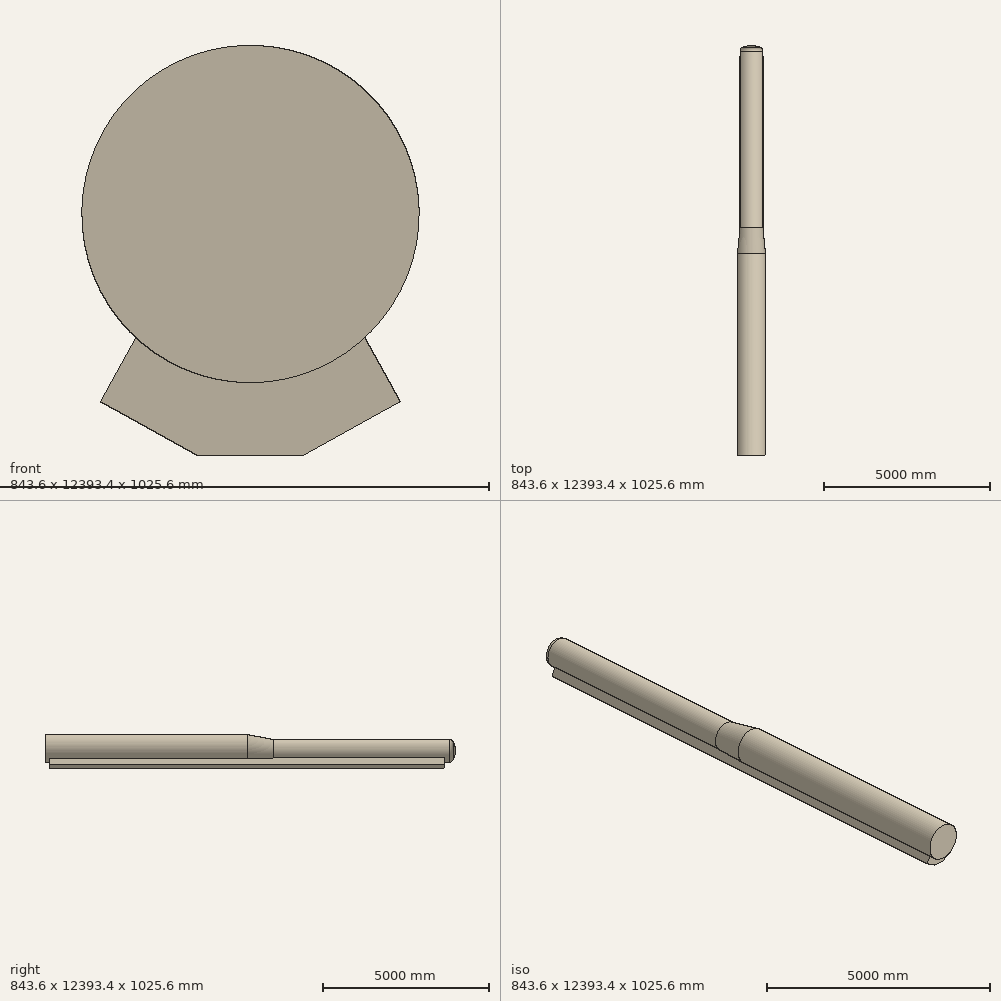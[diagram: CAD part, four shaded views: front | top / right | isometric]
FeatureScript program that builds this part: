
annotation { "Feature Type Name" : "Feature", "Feature Type Description" : "" }
export const myFeature = defineFeature(function(context is Context, id is Id, definition is map)
    precondition{}
    {
        {
            var Q0;
            Q0=qCreatedBy(makeId("Front.planeOp"),FACE);
            var sketch = newSketch(context, id + "F0", { "sketchPlane" : qUnion([Q0])});
            skCircle(sketch, "E0", {"center": v(0, 0) * mm, "radius": 421.8 * mm});
            skSolve(sketch);
        }
        {
            var Q0;
            Q0=makeQuery(id+"F0.imprint","IMPRINT",FACE,{"disambiguationData":[TD([[makeQuery(id+"F0.imprint","IMPRINT",EDGE,{"derivedFrom":sQuery(id+"F0.wireOp",EDGE,"E0")}),1.0]])]});
            extrude(context, id + "F1", {"entities" : qUnion([Q0]), "oppositeDirection" : true, "depth" : 6100 * mm, "offsetDistance" : 25 * mm});
        }
        {
            var Q0;
            Q0=makeQuery(id+"F1.opExtrude","CAP_FACE",FACE,{"disambiguationData":[OSD([sQuery(id+"F0.wireOp",EDGE,"E0")])],"isStart":false});
            cPlane(context, id + "F2", {"entities" : qUnion([Q0]), "cplaneType" : CPlaneType.OFFSET, "offset" : 800 * mm, "width" : 150 * mm, "height" : 150 * mm});
        }
        {
            var Q0;
            Q0=qCreatedBy(id+"F2.planeOp",FACE);
            var sketch = newSketch(context, id + "F3", { "sketchPlane" : qUnion([Q0])});
            skCircle(sketch, "E1", {"center": v(0, -76.2) * mm, "radius": 345.6 * mm});
            skSolve(sketch);
        }
        {
            var Q0;
            Q0=makeQuery(id+"F3.imprint","IMPRINT",FACE,{"disambiguationData":[TD([[makeQuery(id+"F3.imprint","IMPRINT",EDGE,{"derivedFrom":sQuery(id+"F3.wireOp",EDGE,"E1")}),1.0]])]});
            extrude(context, id + "F4", {"entities" : qUnion([Q0]), "depth" : 5324 * mm, "offsetDistance" : 25 * mm});
        }
        {
            var Q0;
            Q0=makeQuery(id+"F1.opExtrude","CAP_FACE",FACE,{"disambiguationData":[OSD([sQuery(id+"F0.wireOp",EDGE,"E0")])],"isStart":false});
            var Q1;
            Q1=makeQuery(id+"F4.opExtrude","CAP_FACE",FACE,{"disambiguationData":[OSD([sQuery(id+"F3.wireOp",EDGE,"E1")])],"isStart":true});
            loft(context, id + "F5", {"sheetProfilesArray" : [{ "sheetProfileEntities" : qUnion([Q0]) }, { "sheetProfileEntities" : qUnion([Q1]) }]});
        }
        {
            var Q0;
            Q0=qCreatedBy(makeId("Right.planeOp"),FACE);
            var sketch = newSketch(context, id + "F6", { "sketchPlane" : qUnion([Q0])});
            skLineSegment(sketch, "E2", {"start": v(6419, -76.2) * mm, "end": v(8600.62, -76.2) * mm, "construction": true});
            skLineSegment(sketch, "E3.0", {"start": v(12224, 269.4) * mm, "end": v(12224, -421.8) * mm, "construction": true});
            skLineSegment(sketch, "E4", {"start": v(12224, -76.2) * mm, "end": v(12393.4, -76.2) * mm});
            skLineSegment(sketch, "E5", {"start": v(12224, -76.2) * mm, "end": v(12224, 269.4) * mm});
            skArc(sketch, "E6", {"start": v(12324.27, 210.71) * mm, "mid": v(12282.1, 253.65) * mm, "end": v(12224, 269.4) * mm});
            skLineSegment(sketch, "E7", {"start": v(6900, 269.4) * mm, "end": v(15224, 269.4) * mm, "construction": true});
            skArc(sketch, "E8", {"start": v(12393.4, -76.2) * mm, "mid": v(12375.87, 71.36) * mm, "end": v(12324.27, 210.71) * mm});
            skSolve(sketch);
        }
        {
            var Q0;
            Q0 = qSketchRegion(id + "F6", true);
            var Q1;
            Q1=sQuery(id+"F6.wireOp",EDGE,"E2");
            revolve(context, id + "F7", {"operationType" : NewBodyOperationType.ADD, "entities" : qUnion([Q0]), "axis" : qUnion([Q1]), "revolveType" : RevolveType.FULL});
        }
        {
            var Q0;
            Q0=makeQuery(id+"F1.opExtrude","CAP_FACE",FACE,{"disambiguationData":[OSD([sQuery(id+"F0.wireOp",EDGE,"E0")])],"isStart":true});
            cPlane(context, id + "F8", {"entities" : qUnion([Q0]), "cplaneType" : CPlaneType.OFFSET, "offset" : 133 * mm, "oppositeDirection" : true, "width" : 150 * mm, "height" : 150 * mm});
        }
        {
            var Q0;
            Q0=qCreatedBy(id+"F8.planeOp",FACE);
            var sketch = newSketch(context, id + "F9", { "sketchPlane" : qUnion([Q0])});
            skLineSegment(sketch, "E9", {"start": v(0, 500.87) * mm, "end": v(0, -792.59) * mm, "construction": true});
            skLineSegment(sketch, "E10", {"start": v(0, 206.66) * mm, "end": v(-374.77, -469.45) * mm});
            skLineSegment(sketch, "E11", {"start": v(0, 206.66) * mm, "end": v(374.77, -469.45) * mm});
            skLineSegment(sketch, "E12", {"start": v(-374.77, -469.45) * mm, "end": v(-132.39, -603.8) * mm});
            skLineSegment(sketch, "E13", {"start": v(-132.39, -603.8) * mm, "end": v(132.4, -603.8) * mm});
            skLineSegment(sketch, "E14", {"start": v(132.4, -603.8) * mm, "end": v(374.77, -469.45) * mm});
            skSolve(sketch);
        }
        {
            var Q0;
            Q0 = qSketchRegion(id + "F9", true);
            extrude(context, id + "F10", {"entities" : qUnion([Q0]), "oppositeDirection" : true, "depth" : 11934 * mm, "offsetDistance" : 25 * mm});
        }
    });
